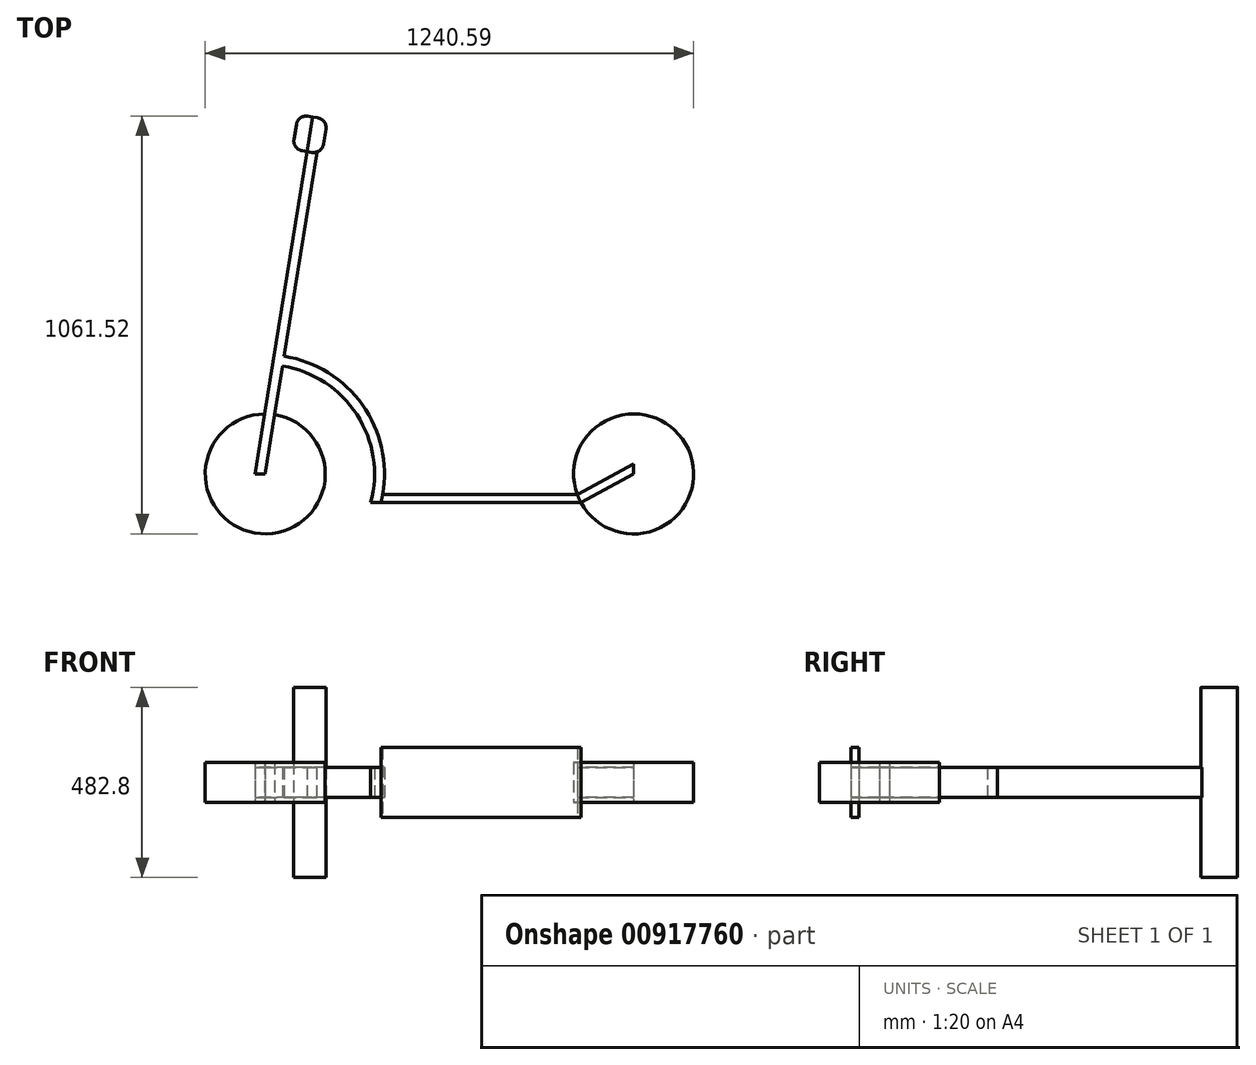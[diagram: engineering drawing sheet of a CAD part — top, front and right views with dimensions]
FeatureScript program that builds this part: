
annotation { "Feature Type Name" : "Feature", "Feature Type Description" : "" }
export const myFeature = defineFeature(function(context is Context, id is Id, definition is map)
    precondition{}
    {
        {
            var Q0;
            Q0=qCreatedBy(makeId("Top.planeOp"),FACE);
            var sketch = newSketch(context, id + "F0", { "sketchPlane" : qUnion([Q0])});
            skCircle(sketch, "E0", {"center": v(0, 0) * mm, "radius": 152.4 * mm});
            skLineSegment(sketch, "E1", {"start": v(0, 0) * mm, "end": v(-133.83, -72.91) * mm});
            skLineSegment(sketch, "E2", {"start": v(-133.83, -72.91) * mm, "end": v(-641.83, -72.91) * mm});
            skCircle(sketch, "E3", {"center": v(-935.8, 0) * mm, "radius": 152.4 * mm});
            skArc(sketch, "E4", {"start": v(-641.83, -72.91) * mm, "mid": v(-683.1, 166.97) * mm, "end": v(-887.58, 299.01) * mm});
            skLineSegment(sketch, "E5", {"start": v(-935.8, 0) * mm, "end": v(-804.39, 814.97) * mm});
            skLineSegment(sketch, "E6", {"start": v(-804.39, 814.97) * mm, "end": v(-829.46, 819.02) * mm});
            skLineSegment(sketch, "E7", {"start": v(-829.46, 819.02) * mm, "end": v(-961.52, 0) * mm});
            skLineSegment(sketch, "E8", {"start": v(-961.52, 0) * mm, "end": v(-935.8, 0) * mm});
            skArc(sketch, "E9", {"start": v(-668.07, -72.91) * mm, "mid": v(-702.56, 150.32) * mm, "end": v(-891.62, 273.93) * mm});
            skLineSegment(sketch, "E10", {"start": v(-641.83, -72.91) * mm, "end": v(-668.07, -72.91) * mm});
            skLineSegment(sketch, "E11", {"start": v(-143.06, -52.54) * mm, "end": v(0, 25.4) * mm});
            skLineSegment(sketch, "E12", {"start": v(0, 25.4) * mm, "end": v(0, 0) * mm});
            skLineSegment(sketch, "E13", {"start": v(-143.06, -52.54) * mm, "end": v(-637.5, -52.54) * mm});
            skSolve(sketch);
        }
        {
            var Q0;
            {var subQ5=sQuery(id+"F0.wireOp",EDGE,"E8");Q0=makeQuery(id+"F0.imprint","IMPRINT",FACE,{"disambiguationData":[TD([[makeQuery(id+"F0.imprint","IMPRINT",EDGE,{"derivedFrom":subQ5}),-1.0]])]});}
            var Q1;
            {var subQ0=sQuery(id+"F0.wireOp",EDGE,"E1");Q1=makeQuery(id+"F0.imprint","IMPRINT",FACE,{"disambiguationData":[TD([[makeQuery(id+"F0.imprint","IMPRINT",EDGE,{"derivedFrom":subQ0}),1.0]])]});}
            extrude(context, id + "F1", {"entities" : qUnion([Q0, Q1]), "depth" : 50.8 * mm, "offsetDistance" : 25.4 * mm, "hasSecondDirection" : true, "secondDirectionOppositeDirection" : true, "secondDirectionDepth" : 50.8 * mm});
        }
        {
            var Q0;
            {var subQ2=sQuery(id+"F0.wireOp",EDGE,"E6");Q0=makeQuery(id+"F0.imprint","IMPRINT",FACE,{"disambiguationData":[TD([[makeQuery(id+"F0.imprint","IMPRINT",EDGE,{"derivedFrom":subQ2}),1.0]])]});}
            var Q1;
            {var subQ5=sQuery(id+"F0.wireOp",EDGE,"E8");Q1=makeQuery(id+"F0.imprint","IMPRINT",FACE,{"disambiguationData":[TD([[makeQuery(id+"F0.imprint","IMPRINT",EDGE,{"derivedFrom":subQ5}),1.0]])]});}
            var Q2;
            {var subQ3=sQuery(id+"F0.wireOp",EDGE,"E9");Q2=makeQuery(id+"F0.imprint","IMPRINT",FACE,{"disambiguationData":[TD([[makeQuery(id+"F0.imprint","IMPRINT",EDGE,{"derivedFrom":subQ3}),-1.0]])]});}
            var Q3;
            {var subQ0=sQuery(id+"F0.wireOp",EDGE,"E1");Q3=makeQuery(id+"F0.imprint","IMPRINT",FACE,{"disambiguationData":[TD([[makeQuery(id+"F0.imprint","IMPRINT",EDGE,{"derivedFrom":subQ0}),-1.0]])]});}
            extrude(context, id + "F2", {"entities" : qUnion([Q0, Q1, Q2, Q3]), "depth" : 38.1 * mm, "offsetDistance" : 25.4 * mm, "hasSecondDirection" : true, "secondDirectionOppositeDirection" : true, "secondDirectionDepth" : 38.1 * mm});
        }
        {
            var Q0;
            {var subQ0=sQuery(id+"F0.wireOp",EDGE,"E2");Q0=makeQuery(id+"F0.imprint","IMPRINT",FACE,{"disambiguationData":[TD([[makeQuery(id+"F0.imprint","IMPRINT",EDGE,{"derivedFrom":subQ0}),-1.0]])]});}
            extrude(context, id + "F3", {"entities" : qUnion([Q0]), "depth" : 88.9 * mm, "offsetDistance" : 25.4 * mm, "hasSecondDirection" : true, "secondDirectionOppositeDirection" : true, "secondDirectionDepth" : 88.9 * mm});
        }
        {
            var Q0;
            Q0=sQuery(id+"F0.wireOp",VERTEX,"E6.end");
            var Q1;
            Q1=sQuery(id+"F0.wireOp",EDGE,"E7");
            cPlane(context, id + "F4", {"entities" : qUnion([Q0, Q1]), "cplaneType" : CPlaneType.CURVE_POINT, "offset" : 25.4 * mm, "width" : 152.4 * mm, "height" : 152.4 * mm});
        }
        {
            var Q0;
            Q0=qCreatedBy(id+"F4.planeOp",FACE);
            var sketch = newSketch(context, id + "F5", { "sketchPlane" : qUnion([Q0])});
            skLineSegment(sketch, "E14", {"start": v(-2218.91, 0) * mm, "end": v(-2218.91, -368.33) * mm});
            skLineSegment(sketch, "E15", {"start": v(-2218.91, -368.33) * mm, "end": v(-2218.91, 114.27) * mm});
            skLineSegment(sketch, "E16", {"start": v(-949.2, 0) * mm, "end": v(-949.2, -241.3) * mm});
            skLineSegment(sketch, "E17", {"start": v(-949.2, 241.5) * mm, "end": v(-949.2, 0.2) * mm});
            skLineSegment(sketch, "E18", {"start": v(-911.1, 241.3) * mm, "end": v(-911.1, 0) * mm});
            skLineSegment(sketch, "E19", {"start": v(-911.1, 0) * mm, "end": v(-911.1, -241.3) * mm});
            skLineSegment(sketch, "E20", {"start": v(-949.2, -241.3) * mm, "end": v(-911.1, -241.3) * mm});
            skLineSegment(sketch, "E21", {"start": v(-949.2, 241.5) * mm, "end": v(-911.1, 241.3) * mm});
            skLineSegment(sketch, "E22", {"start": v(-987.3, 241.3) * mm, "end": v(-987.3, 0) * mm});
            skLineSegment(sketch, "E23", {"start": v(-987.3, 241.3) * mm, "end": v(-949.2, 241.5) * mm});
            skLineSegment(sketch, "E24", {"start": v(-987.3, 0) * mm, "end": v(-987.3, -241.3) * mm});
            skLineSegment(sketch, "E25", {"start": v(-987.3, -241.3) * mm, "end": v(-949.2, -241.3) * mm});
            skSolve(sketch);
        }
        {
            var Q0;
            Q0=makeQuery(id+"F5.imprint","IMPRINT",FACE,{"disambiguationData":[TD([[makeQuery(id+"F5.imprint","IMPRINT",EDGE,{"derivedFrom":sQuery(id+"F5.wireOp",EDGE,"E18")}),-1.0]])]});
            extrude(context, id + "F6", {"entities" : qUnion([Q0]), "operationType" : NewBodyOperationType.ADD, "oppositeDirection" : true, "depth" : 88.9 * mm, "offsetDistance" : 25.4 * mm});
        }
        {
            var Q0;
            Q0=makeQuery(id+"F6.opExtrude","CAP_EDGE",EDGE,{"disambiguationData":[OSD([sQuery(id+"F5.wireOp",EDGE,"E18"),sQuery(id+"F5.wireOp",EDGE,"E19")])],"isStart":false});
            var Q1;
            Q1=makeQuery(id+"F6.opExtrude","CAP_EDGE",EDGE,{"disambiguationData":[OSD([sQuery(id+"F5.wireOp",EDGE,"E18"),sQuery(id+"F5.wireOp",EDGE,"E19")])],"isStart":true});
            var Q2;
            Q2=makeQuery(id+"F6.opExtrude","CAP_EDGE",EDGE,{"disambiguationData":[OSD([sQuery(id+"F5.wireOp",EDGE,"E22"),sQuery(id+"F5.wireOp",EDGE,"E24")])],"isStart":false});
            var Q3;
            Q3=makeQuery(id+"F6.opExtrude","CAP_EDGE",EDGE,{"disambiguationData":[OSD([sQuery(id+"F5.wireOp",EDGE,"E22"),sQuery(id+"F5.wireOp",EDGE,"E24")])],"isStart":true});
            fillet(context, id + "F7", {"entities" : qUnion([Q0, Q1, Q2, Q3]), "radius" : 25.4 * mm, "tangentPropagation" : true, "allowEdgeOverflow" : false});
        }
    });
